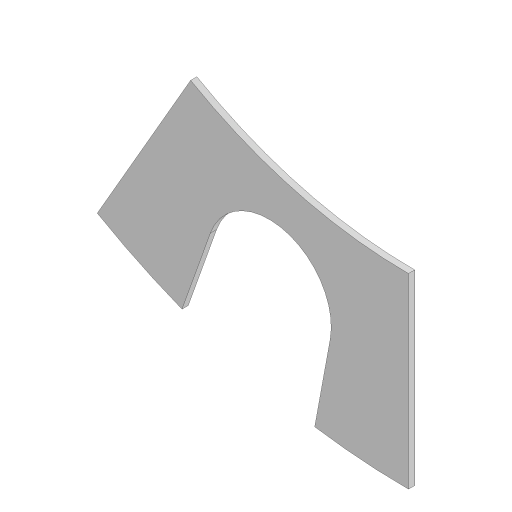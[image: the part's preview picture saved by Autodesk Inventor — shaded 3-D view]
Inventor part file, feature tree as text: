
AUTODESK INVENTOR PART (.ipt)
format: ipt  version: 2023 (Build 270158000, 158)  size: 104,448 bytes
history: native  units: mm
features: extrude x1, sketch x1
ambient origin geometry x8: Origin, YZ Plane, XZ Plane, XY Plane, X Axis, Y Axis, Z Axis, Center Point
bodies: Body1 (feature_tree)
feature tree (2):
  extrude  "押し出し2"  Depth=200.0mm
  sketch  "スケッチ1"
